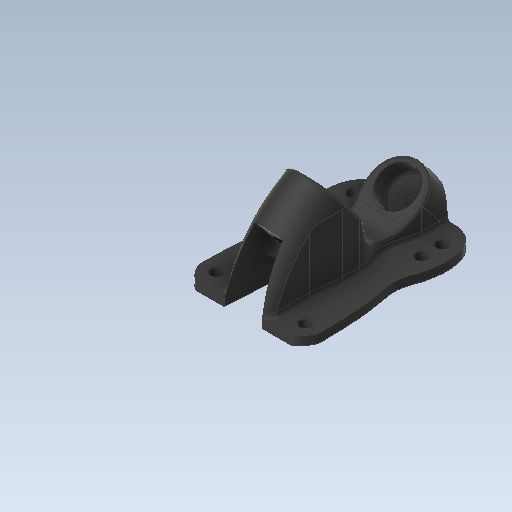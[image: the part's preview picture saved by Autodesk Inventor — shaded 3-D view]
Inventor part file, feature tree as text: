
AUTODESK INVENTOR PART (.ipt)
format: ipt  version: 2020.1 (Build 241239000, 239)  size: 4,587,520 bytes
history: native  units: mm
features: sketch x10, extrude x7, fillet x6, other x5, plane x2, revolve x1, emboss x1, loft x1
ambient origin geometry x8: Origin, YZ Plane, XZ Plane, XY Plane, X Axis, Y Axis, Z Axis, Center Point
bodies: Solid1 (feature_tree)
feature tree (33):
  extrude  "Extrusion8"  Depth=87.0mm
  extrude  "Extrusion11"  Depth=49.0mm
  sketch  "Sketch21"  dims[d14=41.3mm d15=49.0mm d16=57.0mm]
  fillet  "Fillet10"  Radius=57.0mm
  extrude  "Extrusion12"  Depth=80.0mm
  extrude  "Extrusion13"  Depth=20.0mm
  fillet  "Fillet11"  Radius=40.0mm
  extrude  "Extrusion14"  Depth=3.0mm
  extrude  "Extrusion15"  Depth=64.0mm
  plane  "Work Plane14"
  revolve  "Revolution2"  [1 undecoded]
  extrude  "Extrusion16"  Depth=12.5mm
  fillet  "Fillet12"  Radius=25.0mm
  fillet  "Fillet13"  Radius=25.0mm
  emboss  "Emboss2"
  plane  "Work Plane15"
  other  "Work Axis4"
  other  "Work Point1"
  loft  "Loft3"
  fillet  "Fillet16"  Radius=25.0mm
  fillet  "Fillet17"  Radius=11.0mm
  other  "Image6"
  sketch  "Sketch20"  dims[d5=5.5mm d6=5.5mm d7=5.5mm d10=54.0mm d11=63.5mm d13=87.0mm]
  other  "Image10"
  sketch  "Sketch22"  dims[d17=55.0mm d345=80.0mm]
  sketch  "Sketch23"  dims[d380=4.0mm d381=0.0mm d568=20.0mm d571=40.0mm]
  sketch  "Sketch25"  dims[d583=7.0mm d589=3.0mm]
  sketch  "Sketch26"  dims[d608=3.5mm d609=64.0mm]
  other  "Work Axis3"
  sketch  "Sketch27"  dims[d612=6.747409mm d634=12.0mm]
  sketch  "Sketch29"  dims[d646=25.0mm d647=0.0mm d651=12.5mm d652=25.0mm d653=0.0mm d654=25.0mm d655=0.0mm]
  sketch  "Sketch30"  dims[d656=12.5mm d666=9.0mm d668=25.0mm d669=0.0mm d670=11.0mm]
  sketch  "Sketch31"  dims[d671=18.0mm d672=12.0mm d673=0.0mm d674=90.0deg d675=90.0deg d676=19.0mm d677=0.0mm d678=0.0mm d679=1.0mm d680=2.0mm d682=1.0mm d683=0.0mm d684=-21.5mm d685=6.5mm d693=1.0mm d694=0.0mm d695=90.0deg d696=0.0mm d697=90.0deg d698=2.0mm d699=0.5mm d700=9.5mm d703=23.0mm]
note: 1 required parameter value undecoded (feature->parameter linkage not recoverable at this tier; creation-order binding heuristic only, values carry confidence <= 0.55)
